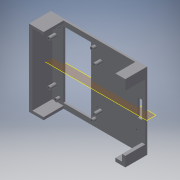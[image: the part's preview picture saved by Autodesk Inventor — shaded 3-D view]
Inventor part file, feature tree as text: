
AUTODESK INVENTOR PART (.ipt)
format: ipt  version: 2019 (Build 230136000, 136)  size: 241,664 bytes
history: native  units: mm
features: sketch x7, reference x6, extrude x4, other x4, plane x3, hole x3, mirror x1, projected_geometry x1
ambient origin geometry x8: Origin, YZ Plane, XZ Plane, XY Plane, X Axis, Y Axis, Z Axis, Center Point
bodies: Solid1 (feature_tree)
feature tree (29):
  extrude  "Extrusion1"  Depth=145.0mm
  sketch  "Sketch2"  dims[d2=8.0mm d3=1.0mm]
  plane  "Work Plane1"
  extrude  "Extrusion2"  Depth=1.0mm
  hole  "Hole1"  [1 undecoded]
  hole  "Hole2"  [1 undecoded]
  sketch  "Sketch5"  dims[d10=2.459mm d11=4.0mm d12=6.3mm d13=2.0mm d14=90.0deg d15=5.0mm d16=20.594885mm]
  plane  "Work Plane2"
  extrude  "Extrusion3"  Depth=1.0mm
  hole  "Hole3"  [1 undecoded]
  plane  "Work Plane3"
  mirror  "Mirror1"
  extrude  "Extrusion4"  Depth=22.0mm
  sketch  "Sketch1"  dims[d0=115.0mm d1=145.0mm]
  reference  "Reference1"
  reference  "Reference2"
  reference  "Reference3"
  sketch  "Sketch3"  dims[d4=0.75mm d5=3.0mm d6=0.0mm]
  reference  "Reference4"
  sketch  "Sketch4"  dims[d7=1.0mm d8=3.0mm d9=0.0mm]
  reference  "Reference5"
  reference  "Reference6"
  sketch  "Sketch6"  dims[d17=2.013mm d18=5.0mm d19=6.3mm d20=2.0mm d21=90.0deg d22=7.6mm d23=20.594885mm d24=1.0mm]
  sketch  "Sketch7"  dims[d25=3.0mm d26=0.0mm d27=2.459mm d28=6.0mm d29=6.3mm d30=2.0mm d31=90.0deg d32=8.8mm d33=20.594885mm d34=5.0mm d35=22.0mm d36=4.0mm d37=15.0mm d38=5.0mm d39=30.0mm d40=0.0mm]
  projected_geometry  "Projected Loop1"
  other  "Assembly1"
  other  "LCD Screen:1"
  other  "Keypad:1"
  other  "PCB:1"
note: 3 required parameter values undecoded (feature->parameter linkage not recoverable at this tier; creation-order binding heuristic only, values carry confidence <= 0.55)
